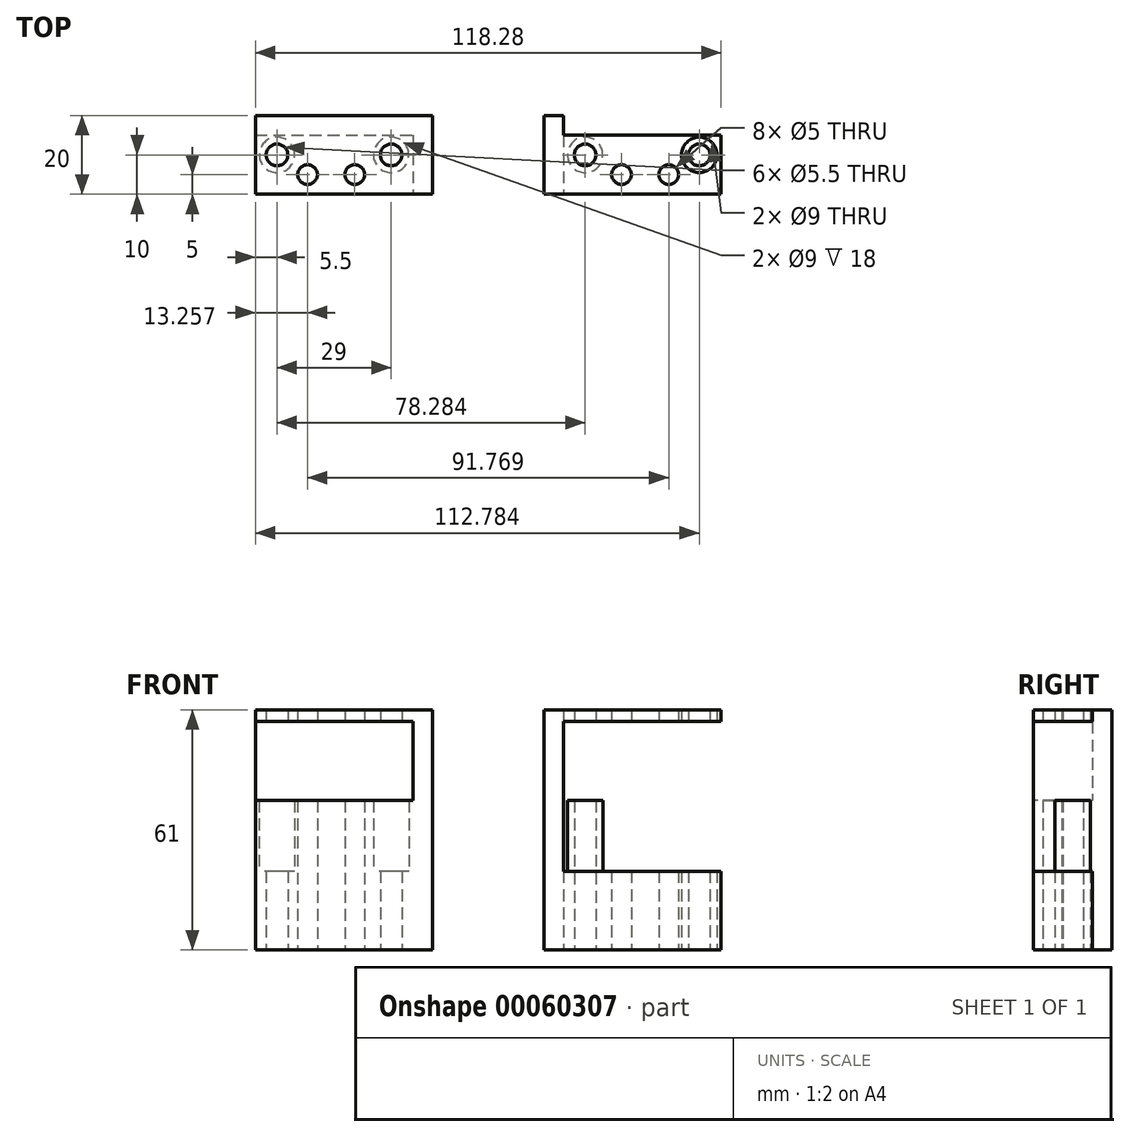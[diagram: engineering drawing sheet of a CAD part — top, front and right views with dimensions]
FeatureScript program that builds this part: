
annotation { "Feature Type Name" : "Feature", "Feature Type Description" : "" }
export const myFeature = defineFeature(function(context is Context, id is Id, definition is map)
    precondition{}
    {
        {
            var Q0;
            Q0=qCreatedBy(makeId("Top.planeOp"),FACE);
            var sketch = newSketch(context, id + "F0", { "sketchPlane" : qUnion([Q0])});
            skLineSegment(sketch, "E0.bottom", {"start": v(-20, 10) * mm, "end": v(20, 10) * mm});
            skLineSegment(sketch, "E0.top", {"start": v(-20, -10) * mm, "end": v(20, -10) * mm});
            skLineSegment(sketch, "E0.left", {"start": v(-20, 10) * mm, "end": v(-20, -10) * mm});
            skLineSegment(sketch, "E0.right", {"start": v(20, 10) * mm, "end": v(20, -10) * mm});
            skLineSegment(sketch, "E1", {"start": v(0, 10) * mm, "end": v(0, -10) * mm, "construction": true});
            skLineSegment(sketch, "E2.bottom", {"start": v(20, 10) * mm, "end": v(25, 10) * mm});
            skLineSegment(sketch, "E2.top", {"start": v(20, -10) * mm, "end": v(25, -10) * mm});
            skLineSegment(sketch, "E2.right", {"start": v(25, 10) * mm, "end": v(25, -10) * mm});
            skLineSegment(sketch, "E3.top", {"start": v(-20, 5) * mm, "end": v(20, 5) * mm});
            skLineSegment(sketch, "E3.left", {"start": v(-20, 10) * mm, "end": v(-20, 5) * mm});
            skLineSegment(sketch, "E3.right", {"start": v(20, 10) * mm, "end": v(20, 5) * mm});
            skCircle(sketch, "E4", {"center": v(-6.74, -5) * mm, "radius": 2.5 * mm});
            skCircle(sketch, "E5", {"center": v(5.26, -5) * mm, "radius": 2.5 * mm});
            skLineSegment(sketch, "E6", {"start": v(25, 0) * mm, "end": v(-20, 0) * mm, "construction": true});
            skCircle(sketch, "E7", {"center": v(14.5, 0) * mm, "radius": 4.5 * mm});
            skCircle(sketch, "E8", {"center": v(-14.5, 0) * mm, "radius": 4.5 * mm});
            skCircle(sketch, "E9", {"center": v(14.5, 0) * mm, "radius": 2.75 * mm});
            skCircle(sketch, "E10", {"center": v(-14.5, 0) * mm, "radius": 2.75 * mm});
            skLineSegment(sketch, "E11", {"start": v(39.14, 10) * mm, "end": v(39.14, -10) * mm});
            skLineSegment(sketch, "E12.MirrorCS", {"start": v(98.28, 10) * mm, "end": v(58.28, 10) * mm});
            skLineSegment(sketch, "E13.MirrorCS", {"start": v(58.28, 10) * mm, "end": v(58.28, -10) * mm});
            skCircle(sketch, "E14.MirrorC", {"center": v(63.78, 0) * mm, "radius": 4.5 * mm});
            skCircle(sketch, "E15.MirrorC", {"center": v(92.78, 0) * mm, "radius": 2.75 * mm});
            skCircle(sketch, "E16.MirrorC", {"center": v(85.03, -5) * mm, "radius": 2.5 * mm});
            skCircle(sketch, "E17.MirrorC", {"center": v(92.78, 0) * mm, "radius": 4.5 * mm});
            skCircle(sketch, "E18.MirrorC", {"center": v(73.03, -5) * mm, "radius": 2.5 * mm});
            skLineSegment(sketch, "E19.MirrorCS", {"start": v(78.28, 10) * mm, "end": v(78.28, -10) * mm, "construction": true});
            skLineSegment(sketch, "E20.MirrorCS", {"start": v(53.28, 0) * mm, "end": v(98.28, 0) * mm, "construction": true});
            skLineSegment(sketch, "E21.MirrorCS", {"start": v(98.28, -10) * mm, "end": v(58.28, -10) * mm});
            skLineSegment(sketch, "E22.MirrorCS", {"start": v(98.28, 10) * mm, "end": v(98.28, -10) * mm});
            skLineSegment(sketch, "E23.MirrorCS", {"start": v(58.28, 10) * mm, "end": v(53.28, 10) * mm});
            skLineSegment(sketch, "E24.MirrorCS", {"start": v(58.28, -10) * mm, "end": v(53.28, -10) * mm});
            skLineSegment(sketch, "E25.MirrorCS", {"start": v(53.28, 10) * mm, "end": v(53.28, -10) * mm});
            skLineSegment(sketch, "E26.MirrorCS", {"start": v(98.28, 5) * mm, "end": v(58.28, 5) * mm});
            skLineSegment(sketch, "E27.MirrorCS", {"start": v(98.28, 10) * mm, "end": v(98.28, 5) * mm});
            skLineSegment(sketch, "E28.MirrorCS", {"start": v(58.28, 10) * mm, "end": v(58.28, 5) * mm});
            skCircle(sketch, "E29.MirrorC", {"center": v(63.78, 0) * mm, "radius": 2.75 * mm});
            skSolve(sketch);
        }
        {
            var Q0;
            Q0=makeQuery(id+"F0.imprint","IMPRINT",FACE,{"disambiguationData":[TD([[makeQuery(id+"F0.imprint","IMPRINT",EDGE,{"derivedFrom":sQuery(id+"F0.wireOp",EDGE,"E0.top")}),1.0]])]});
            var Q1;
            Q1=makeQuery(id+"F0.imprint","IMPRINT",FACE,{"disambiguationData":[TD([[makeQuery(id+"F0.imprint","IMPRINT",EDGE,{"derivedFrom":sQuery(id+"F0.wireOp",EDGE,"E14.MirrorC")}),1.0]])]});
            extrude(context, id + "F1", {"entities" : qUnion([Q0, Q1]), "depth" : 38 * mm});
        }
        {
            var Q0;
            Q0=makeQuery(id+"F0.imprint","IMPRINT",FACE,{"disambiguationData":[TD([[makeQuery(id+"F0.imprint","IMPRINT",EDGE,{"derivedFrom":sQuery(id+"F0.wireOp",EDGE,"E2.bottom")}),-1.0]])]});
            var Q1;
            Q1=makeQuery(id+"F0.imprint","IMPRINT",FACE,{"disambiguationData":[TD([[makeQuery(id+"F0.imprint","IMPRINT",EDGE,{"derivedFrom":sQuery(id+"F0.wireOp",EDGE,"E0.bottom")}),-1.0]])]});
            var Q2;
            Q2=makeQuery(id+"F0.imprint","IMPRINT",FACE,{"disambiguationData":[TD([[makeQuery(id+"F0.imprint","IMPRINT",EDGE,{"derivedFrom":sQuery(id+"F0.wireOp",EDGE,"E23.MirrorCS")}),1.0]])]});
            var Q3;
            Q3=makeQuery(id+"F0.imprint","IMPRINT",FACE,{"disambiguationData":[TD([[makeQuery(id+"F0.imprint","IMPRINT",EDGE,{"derivedFrom":sQuery(id+"F0.wireOp",EDGE,"E12.MirrorCS")}),1.0]])]});
            extrude(context, id + "F2", {"entities" : qUnion([Q0, Q1, Q2, Q3]), "operationType" : NewBodyOperationType.ADD, "depth" : 61 * mm});
        }
        {
            var Q0;
            Q0=makeQuery(id+"F0.imprint","IMPRINT",FACE,{"disambiguationData":[TD([[makeQuery(id+"F0.imprint","IMPRINT",EDGE,{"derivedFrom":sQuery(id+"F0.wireOp",EDGE,"E0.top")}),1.0]])]});
            var Q1;
            Q1=makeQuery(id+"F0.imprint","IMPRINT",FACE,{"disambiguationData":[TD([[makeQuery(id+"F0.imprint","IMPRINT",EDGE,{"derivedFrom":sQuery(id+"F0.wireOp",EDGE,"E14.MirrorC")}),1.0]])]});
            extrude(context, id + "F3", {"entities" : qUnion([Q0, Q1]), "operationType" : NewBodyOperationType.ADD, "depth" : 61 * mm, "hasSecondDirection" : true, "secondDirectionOppositeDirection" : false, "secondDirectionDepth" : 58 * mm});
        }
        {
            var Q0;
            Q0=makeQuery(id+"F0.imprint","IMPRINT",FACE,{"disambiguationData":[TD([[makeQuery(id+"F0.imprint","IMPRINT",EDGE,{"derivedFrom":sQuery(id+"F0.wireOp",EDGE,"E8")}),1.0]])]});
            var Q1;
            Q1=makeQuery(id+"F0.imprint","IMPRINT",FACE,{"disambiguationData":[TD([[makeQuery(id+"F0.imprint","IMPRINT",EDGE,{"derivedFrom":sQuery(id+"F0.wireOp",EDGE,"E7")}),1.0]])]});
            var Q2;
            Q2=makeQuery(id+"F0.imprint","IMPRINT",FACE,{"disambiguationData":[TD([[makeQuery(id+"F0.imprint","IMPRINT",EDGE,{"derivedFrom":sQuery(id+"F0.wireOp",EDGE,"E14.MirrorC")}),-1.0]])]});
            var Q3;
            Q3=makeQuery(id+"F0.imprint","IMPRINT",FACE,{"disambiguationData":[TD([[makeQuery(id+"F0.imprint","IMPRINT",EDGE,{"derivedFrom":sQuery(id+"F0.wireOp",EDGE,"E15.MirrorC")}),1.0]])]});
            extrude(context, id + "F4", {"entities" : qUnion([Q0, Q1, Q2, Q3]), "operationType" : NewBodyOperationType.ADD, "depth" : 20 * mm});
        }
        {
            var Q0;
            Q0=makeQuery(id+"F0.imprint","IMPRINT",FACE,{"disambiguationData":[TD([[makeQuery(id+"F0.imprint","IMPRINT",EDGE,{"derivedFrom":sQuery(id+"F0.wireOp",EDGE,"E8")}),1.0]])]});
            var Q1;
            Q1=makeQuery(id+"F0.imprint","IMPRINT",FACE,{"disambiguationData":[TD([[makeQuery(id+"F0.imprint","IMPRINT",EDGE,{"derivedFrom":sQuery(id+"F0.wireOp",EDGE,"E7")}),1.0]])]});
            var Q2;
            Q2=makeQuery(id+"F0.imprint","IMPRINT",FACE,{"disambiguationData":[TD([[makeQuery(id+"F0.imprint","IMPRINT",EDGE,{"derivedFrom":sQuery(id+"F0.wireOp",EDGE,"E14.MirrorC")}),-1.0]])]});
            var Q3;
            Q3=makeQuery(id+"F0.imprint","IMPRINT",FACE,{"disambiguationData":[TD([[makeQuery(id+"F0.imprint","IMPRINT",EDGE,{"derivedFrom":sQuery(id+"F0.wireOp",EDGE,"E15.MirrorC")}),1.0]])]});
            extrude(context, id + "F5", {"entities" : qUnion([Q0, Q1, Q2, Q3]), "operationType" : NewBodyOperationType.ADD, "depth" : 61 * mm, "hasSecondDirection" : true, "secondDirectionOppositeDirection" : false, "secondDirectionDepth" : 58 * mm});
        }
    });
